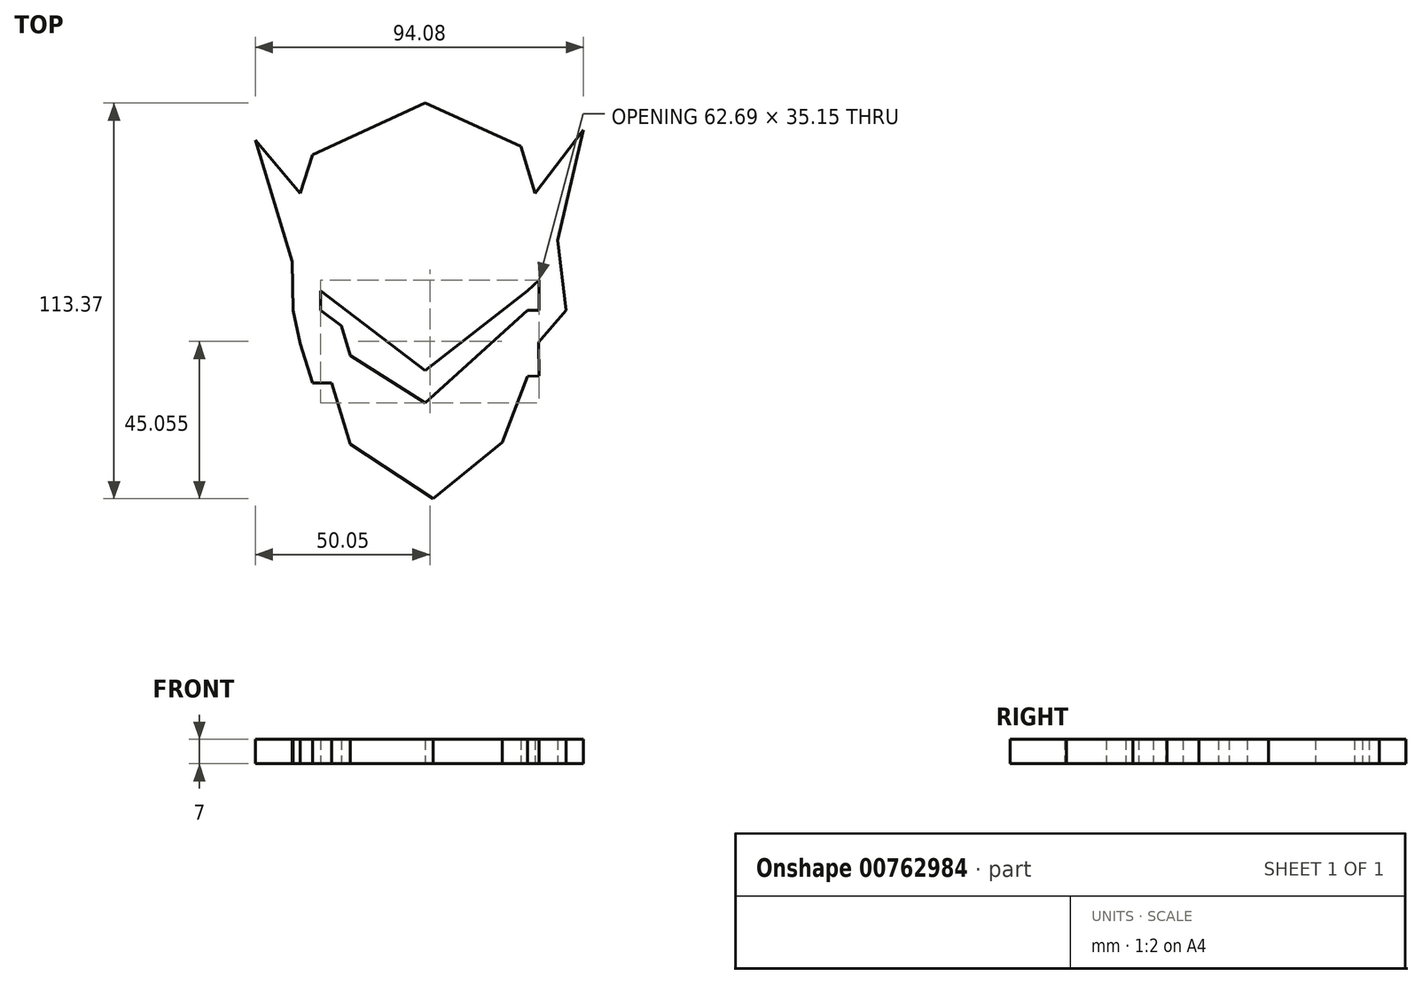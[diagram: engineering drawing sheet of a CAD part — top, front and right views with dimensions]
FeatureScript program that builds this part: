
annotation { "Feature Type Name" : "Feature", "Feature Type Description" : "" }
export const myFeature = defineFeature(function(context is Context, id is Id, definition is map)
    precondition{}
    {
        {
            var Q0;
            Q0=qCreatedBy(makeId("Top.planeOp"),FACE);
            var sketch = newSketch(context, id + "F0", { "sketchPlane" : qUnion([Q0])});
            skLineSegment(sketch, "E0", {"start": v(-38.19, 13.87) * mm, "end": v(-48.76, 48.76) * mm});
            skLineSegment(sketch, "E1", {"start": v(-48.76, 48.76) * mm, "end": v(-35.8, 33.43) * mm});
            skLineSegment(sketch, "E2", {"start": v(-35.8, 33.43) * mm, "end": v(-32.37, 44.53) * mm});
            skLineSegment(sketch, "E3", {"start": v(-32.37, 44.53) * mm, "end": v(0, 59.33) * mm});
            skLineSegment(sketch, "E4", {"start": v(0, 59.33) * mm, "end": v(27.35, 46.9) * mm});
            skLineSegment(sketch, "E5", {"start": v(27.35, 46.9) * mm, "end": v(31.44, 33.43) * mm});
            skLineSegment(sketch, "E6", {"start": v(31.44, 33.43) * mm, "end": v(45.32, 51.66) * mm});
            skLineSegment(sketch, "E7", {"start": v(45.32, 51.66) * mm, "end": v(37.92, 19.95) * mm});
            skLineSegment(sketch, "E8", {"start": v(37.92, 19.95) * mm, "end": v(40.3, 0) * mm});
            skLineSegment(sketch, "E9", {"start": v(40.3, 0) * mm, "end": v(32.64, 8.59) * mm});
            skLineSegment(sketch, "E10", {"start": v(32.64, 8.59) * mm, "end": v(29.26, 5.58) * mm});
            skLineSegment(sketch, "E11", {"start": v(29.26, 5.58) * mm, "end": v(0, -17.3) * mm});
            skLineSegment(sketch, "E12", {"start": v(0, -17.3) * mm, "end": v(-30.06, 5.58) * mm});
            skLineSegment(sketch, "E13", {"start": v(-30.06, 5.58) * mm, "end": v(-30.06, 0) * mm});
            skLineSegment(sketch, "E14", {"start": v(-30.06, 0) * mm, "end": v(-24.06, -4.57) * mm});
            skLineSegment(sketch, "E15", {"start": v(-24.06, -4.57) * mm, "end": v(-21.5, -13.04) * mm});
            skLineSegment(sketch, "E16", {"start": v(-21.5, -13.04) * mm, "end": v(0, -26.56) * mm});
            skLineSegment(sketch, "E17", {"start": v(0, -26.56) * mm, "end": v(29.26, 0) * mm});
            skLineSegment(sketch, "E18", {"start": v(32.42, -9.18) * mm, "end": v(32.64, -18.9) * mm});
            skLineSegment(sketch, "E19", {"start": v(32.64, -18.9) * mm, "end": v(29.26, -18.97) * mm});
            skLineSegment(sketch, "E20", {"start": v(29.26, -18.97) * mm, "end": v(22.07, -37.92) * mm});
            skLineSegment(sketch, "E21", {"start": v(22.07, -37.92) * mm, "end": v(2.25, -54.04) * mm});
            skLineSegment(sketch, "E22", {"start": v(2.25, -54.04) * mm, "end": v(-21.5, -38.45) * mm});
            skLineSegment(sketch, "E23", {"start": v(-21.5, -38.45) * mm, "end": v(-26.8, -20.92) * mm});
            skLineSegment(sketch, "E24", {"start": v(-26.8, -20.92) * mm, "end": v(-32.37, -20.92) * mm});
            skLineSegment(sketch, "E25", {"start": v(-32.37, -20.92) * mm, "end": v(-35.8, -9.59) * mm});
            skLineSegment(sketch, "E26", {"start": v(-35.8, -9.59) * mm, "end": v(-30.06, 0) * mm});
            skLineSegment(sketch, "E27", {"start": v(-30.06, 5.58) * mm, "end": v(-32.37, 7.34) * mm});
            skLineSegment(sketch, "E28", {"start": v(-32.37, 7.34) * mm, "end": v(-37.96, 0) * mm});
            skLineSegment(sketch, "E29", {"start": v(-38.19, 13.87) * mm, "end": v(-27.43, 28) * mm});
            skLineSegment(sketch, "E30", {"start": v(-27.43, 28) * mm, "end": v(-21.5, 23.48) * mm});
            skLineSegment(sketch, "E31", {"start": v(-21.5, 23.48) * mm, "end": v(0, 47.17) * mm});
            skLineSegment(sketch, "E32", {"start": v(0, 47.17) * mm, "end": v(19.95, 25.77) * mm});
            skLineSegment(sketch, "E33", {"start": v(19.95, 25.77) * mm, "end": v(22.71, 29.39) * mm});
            skLineSegment(sketch, "E34", {"start": v(22.71, 29.39) * mm, "end": v(37.92, 19.95) * mm});
            skLineSegment(sketch, "E35", {"start": v(-21.5, 13.87) * mm, "end": v(-15.67, 8.59) * mm});
            skLineSegment(sketch, "E36", {"start": v(-17.57, 17.84) * mm, "end": v(-14.4, 13.08) * mm});
            skLineSegment(sketch, "E37", {"start": v(21.8, 17.57) * mm, "end": v(19.07, 15.03) * mm});
            skLineSegment(sketch, "E38", {"start": v(24.97, 8.59) * mm, "end": v(22.66, 5.55) * mm});
            skLineSegment(sketch, "E39", {"start": v(40.3, 0) * mm, "end": v(32.42, -9.18) * mm});
            skLineSegment(sketch, "E40", {"start": v(-37.96, 0) * mm, "end": v(-30.06, 0) * mm});
            skLineSegment(sketch, "E41", {"start": v(-37.96, 0) * mm, "end": v(-35.8, -9.59) * mm});
            skLineSegment(sketch, "E42", {"start": v(-38.19, 13.87) * mm, "end": v(-37.96, 0) * mm});
            skLineSegment(sketch, "E43", {"start": v(32.64, 8.59) * mm, "end": v(32.64, 0) * mm});
            skLineSegment(sketch, "E44", {"start": v(32.64, 0) * mm, "end": v(29.26, 0) * mm});
            skLineSegment(sketch, "E45", {"start": v(32.42, -9.18) * mm, "end": v(29.26, 0) * mm});
            skSolve(sketch);
        }
        {
            var Q0;
            Q0 = qSketchRegion(id + "F0", true);
            extrude(context, id + "F1", {"entities" : qUnion([Q0]), "depth" : 7 * mm, "offsetDistance" : 25 * mm});
        }
    });
